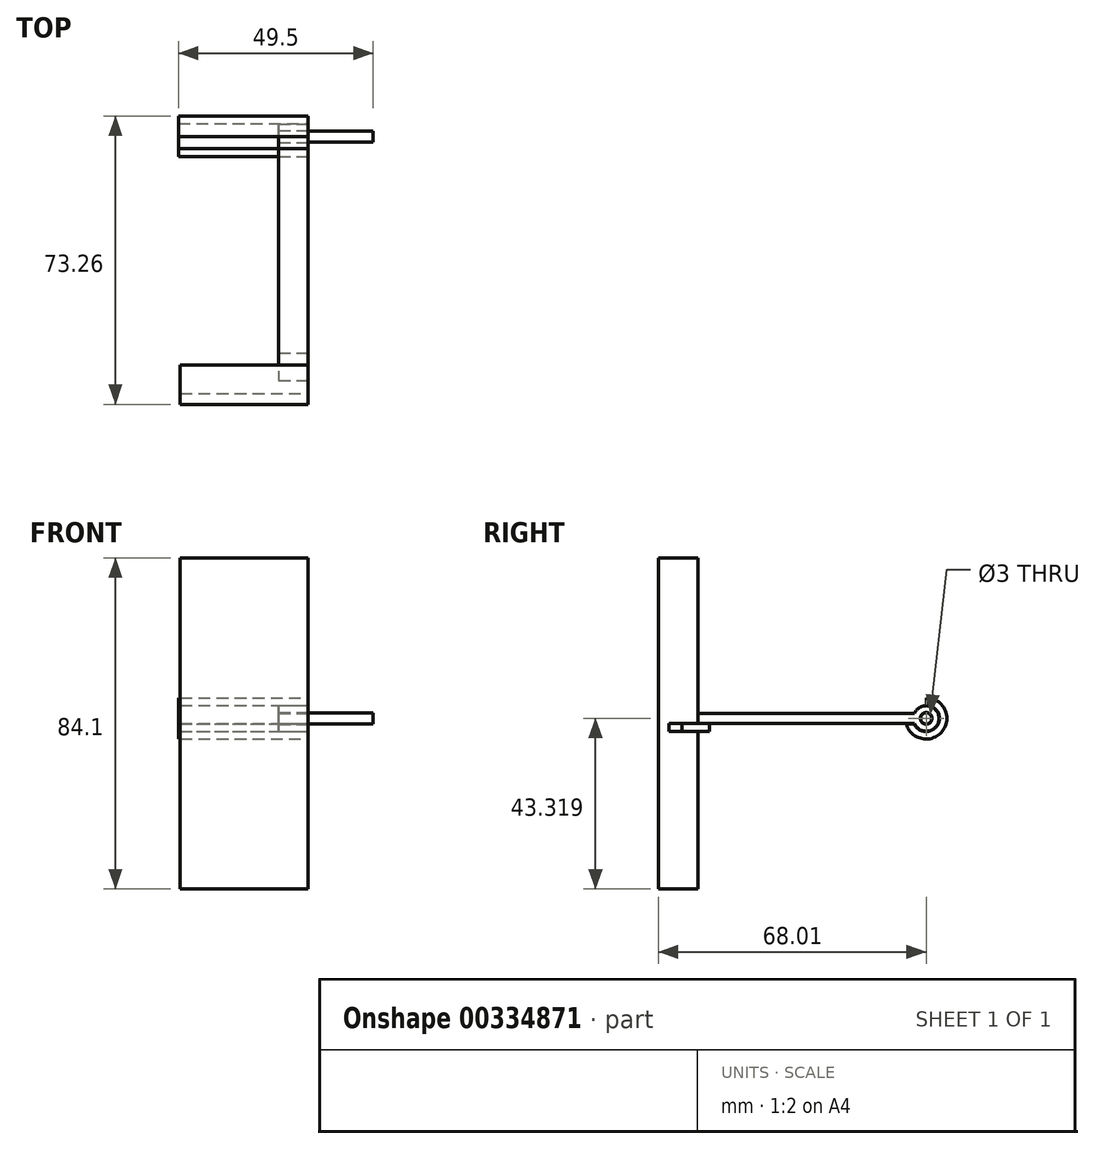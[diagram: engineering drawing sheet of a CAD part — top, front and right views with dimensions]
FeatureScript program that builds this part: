
annotation { "Feature Type Name" : "Feature", "Feature Type Description" : "" }
export const myFeature = defineFeature(function(context is Context, id is Id, definition is map)
    precondition{}
    {
        {
            var Q0;
            Q0=qCreatedBy(makeId("Top.planeOp"),FACE);
            var sketch = newSketch(context, id + "F0", { "sketchPlane" : qUnion([Q0])});
            skLineSegment(sketch, "E0.bottom", {"start": v(8, 0) * mm, "end": v(15.5, 0) * mm});
            skLineSegment(sketch, "E0.top", {"start": v(8, -55) * mm, "end": v(15.5, -55) * mm});
            skLineSegment(sketch, "E0.left", {"start": v(8, 0) * mm, "end": v(8, -55) * mm});
            skLineSegment(sketch, "E0.right", {"start": v(15.5, 0) * mm, "end": v(15.5, -55) * mm});
            skSolve(sketch);
        }
        {
            var Q0;
            Q0 = qSketchRegion(id + "F0", true);
            extrude(context, id + "F1", {"entities" : qUnion([Q0]), "depth" : 2.5 * mm});
        }
        {
            var Q0;
            Q0=makeQuery(id+"F1.opExtrude","SWEPT_FACE",FACE,{"disambiguationData":[OSD([sQuery(id+"F0.wireOp",EDGE,"E0.right")])]});
            var sketch = newSketch(context, id + "F2", { "sketchPlane" : qUnion([Q0])});
            skArc(sketch, "E1", {"start": v(-2.07, -0.1) * mm, "mid": v(7.17, -1.93) * mm, "end": v(3, 6.52) * mm});
            skCircle(sketch, "E2", {"center": v(3, 1.27) * mm, "radius": 1.5 * mm});
            skLineSegment(sketch, "E3", {"start": v(0, 2.5) * mm, "end": v(0, 0) * mm});
            skArc(sketch, "E4", {"start": v(0, 0) * mm, "mid": v(6.25, 1.25) * mm, "end": v(0, 2.5) * mm});
            skPoint(sketch, "E5.orphan", {"position": v(1.2, 0) * mm});
            skArc(sketch, "E6", {"start": v(-0.06, -0.1) * mm, "mid": v(5.81, -0.55) * mm, "end": v(3, 4.62) * mm});
            skLineSegment(sketch, "E7", {"start": v(-2.07, -0.1) * mm, "end": v(-0.06, -0.1) * mm});
            skLineSegment(sketch, "E8.trimOffspring", {"start": v(3, 4.62) * mm, "end": v(3, 6.52) * mm});
            skPoint(sketch, "E9.end.orphan", {"position": v(-2.1, 0) * mm});
            skCircle(sketch, "E10", {"center": v(3, 1.27) * mm, "radius": 1.4 * mm});
            skSolve(sketch);
        }
        {
            var Q0;
            Q0=makeQuery(id+"F2.imprint","IMPRINT",FACE,{"disambiguationData":[TD([[makeQuery(id+"F2.imprint","IMPRINT",EDGE,{"derivedFrom":sQuery(id+"F2.wireOp",EDGE,"E2")}),-1.0]])]});
            extrude(context, id + "F3", {"entities" : qUnion([Q0]), "operationType" : NewBodyOperationType.ADD, "oppositeDirection" : true, "depth" : 7.5 * mm});
        }
        {
            var Q0;
            Q0=sQuery(id+"F2.wireOp",EDGE,"E10");
            extrude(context, id + "F4", {"bodyType" : ToolBodyType.SURFACE, "surfaceEntities" : qUnion([Q0]), "oppositeDirection" : true, "depth" : 40 * mm});
        }
        {
            var Q0;
            Q0=makeQuery(id+"F2.imprint","IMPRINT",FACE,{"disambiguationData":[TD([[makeQuery(id+"F2.imprint","IMPRINT",EDGE,{"derivedFrom":sQuery(id+"F2.wireOp",EDGE,"E1")}),1.0]])]});
            extrude(context, id + "F5", {"entities" : qUnion([Q0]), "oppositeDirection" : true, "depth" : 33 * mm});
        }
        {
            var Q0;
            Q0=makeQuery(id+"F2.imprint","IMPRINT",FACE,{"disambiguationData":[TD([[makeQuery(id+"F2.imprint","IMPRINT",EDGE,{"derivedFrom":sQuery(id+"F2.wireOp",EDGE,"E10")}),1.0]])]});
            extrude(context, id + "F6", {"entities" : qUnion([Q0]), "depth" : 16.5 * mm});
        }
        {
            var Q0;
            Q0=makeQuery(id+"F4.opExtrude","SWEPT_BODY",BODY,{"disambiguationData":[OSD([sQuery(id+"F2.wireOp",EDGE,"E10")])]});
            deleteBodies(context, id + "F7", {"entities" : qUnion([Q0])});
        }
        {
            var Q0;
            {var subQ0=sQuery(id+"F0.wireOp",EDGE,"E0.right");var subQ1=makeQuery(id+"F1.opExtrude","CAP_EDGE",EDGE,{"disambiguationData":[OSD([subQ0])],"isStart":true});Q0=makeQuery(id+"F2.imprint","IMPRINT",FACE,{"disambiguationData":[TD([[makeQuery(id+"F2.imprint","IMPRINT",EDGE,{"derivedFrom":subQ1}),-1.0]])]});}
            var sketch = newSketch(context, id + "F8", { "sketchPlane" : qUnion([Q0])});
            skLineSegment(sketch, "E11.bottom", {"start": v(-52, 0) * mm, "end": v(-59, 0) * mm});
            skLineSegment(sketch, "E11.top", {"start": v(-52, -2.05) * mm, "end": v(-59, -2.05) * mm});
            skLineSegment(sketch, "E11.left", {"start": v(-52, 0) * mm, "end": v(-52, -2.05) * mm});
            skLineSegment(sketch, "E11.right", {"start": v(-59, 0) * mm, "end": v(-59, -2.05) * mm});
            skSolve(sketch);
        }
        {
            var Q0;
            Q0=makeQuery(id+"F8.imprint","IMPRINT",FACE,{"disambiguationData":[TD([[makeQuery(id+"F8.imprint","IMPRINT",EDGE,{"derivedFrom":sQuery(id+"F8.wireOp",EDGE,"E11.top")}),-1.0]])]});
            extrude(context, id + "F9", {"entities" : qUnion([Q0]), "depth" : -7.5 * mm});
        }
        {
            var Q0;
            Q0=makeQuery(id+"F9.opExtrude","CAP_FACE",FACE,{"disambiguationData":[OSD([sQuery(id+"F8.wireOp",EDGE,"E11.bottom"),sQuery(id+"F8.wireOp",EDGE,"E11.top"),sQuery(id+"F8.wireOp",EDGE,"E11.left"),sQuery(id+"F8.wireOp",EDGE,"E11.right")])],"isStart":true});
            var sketch = newSketch(context, id + "F10", { "sketchPlane" : qUnion([Q0])});
            skLineSegment(sketch, "E12.bottom", {"start": v(-55.02, 0) * mm, "end": v(-54.99, 0) * mm});
            skLineSegment(sketch, "E12.top", {"start": v(-55.02, -2.05) * mm, "end": v(-55, -2.05) * mm});
            skLineSegment(sketch, "E13.bottom", {"start": v(-55, -2.05) * mm, "end": v(-62.3, -2.05) * mm});
            skLineSegment(sketch, "E13.top", {"start": v(-55, -42.05) * mm, "end": v(-65, -42.05) * mm});
            skLineSegment(sketch, "E13.left", {"start": v(-55, -2.05) * mm, "end": v(-55, -42.05) * mm});
            skLineSegment(sketch, "E13.right", {"start": v(-65, -2.05) * mm, "end": v(-65, -42.05) * mm});
            skLineSegment(sketch, "E14.MirrorCS", {"start": v(-65, 2.05) * mm, "end": v(-65, 42.05) * mm});
            skLineSegment(sketch, "E15.MirrorCS", {"start": v(-55, 2.05) * mm, "end": v(-55, 42.05) * mm});
            skLineSegment(sketch, "E16.MirrorCS", {"start": v(-55, 42.05) * mm, "end": v(-65, 42.05) * mm});
            skLineSegment(sketch, "E17", {"start": v(-54.99, 0) * mm, "end": v(-62.3, 0) * mm});
            skLineSegment(sketch, "E18", {"start": v(-65, 0) * mm, "end": v(-65, -2.05) * mm});
            skLineSegment(sketch, "E19", {"start": v(-65, 2.05) * mm, "end": v(-65, 0) * mm});
            skLineSegment(sketch, "E20", {"start": v(-54.99, 0) * mm, "end": v(-59, 0) * mm});
            skLineSegment(sketch, "E21", {"start": v(-62.3, -2.05) * mm, "end": v(-62.3, 0) * mm});
            skPoint(sketch, "E22.orphan", {"position": v(-65, -2.05) * mm});
            skLineSegment(sketch, "E23", {"start": v(-55, 2.05) * mm, "end": v(-54.99, 0) * mm});
            skPoint(sketch, "E24.MirrorCS.end.orphan", {"position": v(-65, 2.05) * mm});
            skSolve(sketch);
        }
        {
            var Q0;
            Q0=makeQuery(id+"F10.imprint","IMPRINT",FACE,{"disambiguationData":[TD([[makeQuery(id+"F10.imprint","IMPRINT",EDGE,{"derivedFrom":sQuery(id+"F10.wireOp",EDGE,"E13.top")}),-1.0]])]});
            extrude(context, id + "F11", {"entities" : qUnion([Q0]), "oppositeDirection" : true, "depth" : 32.5 * mm});
        }
    });
